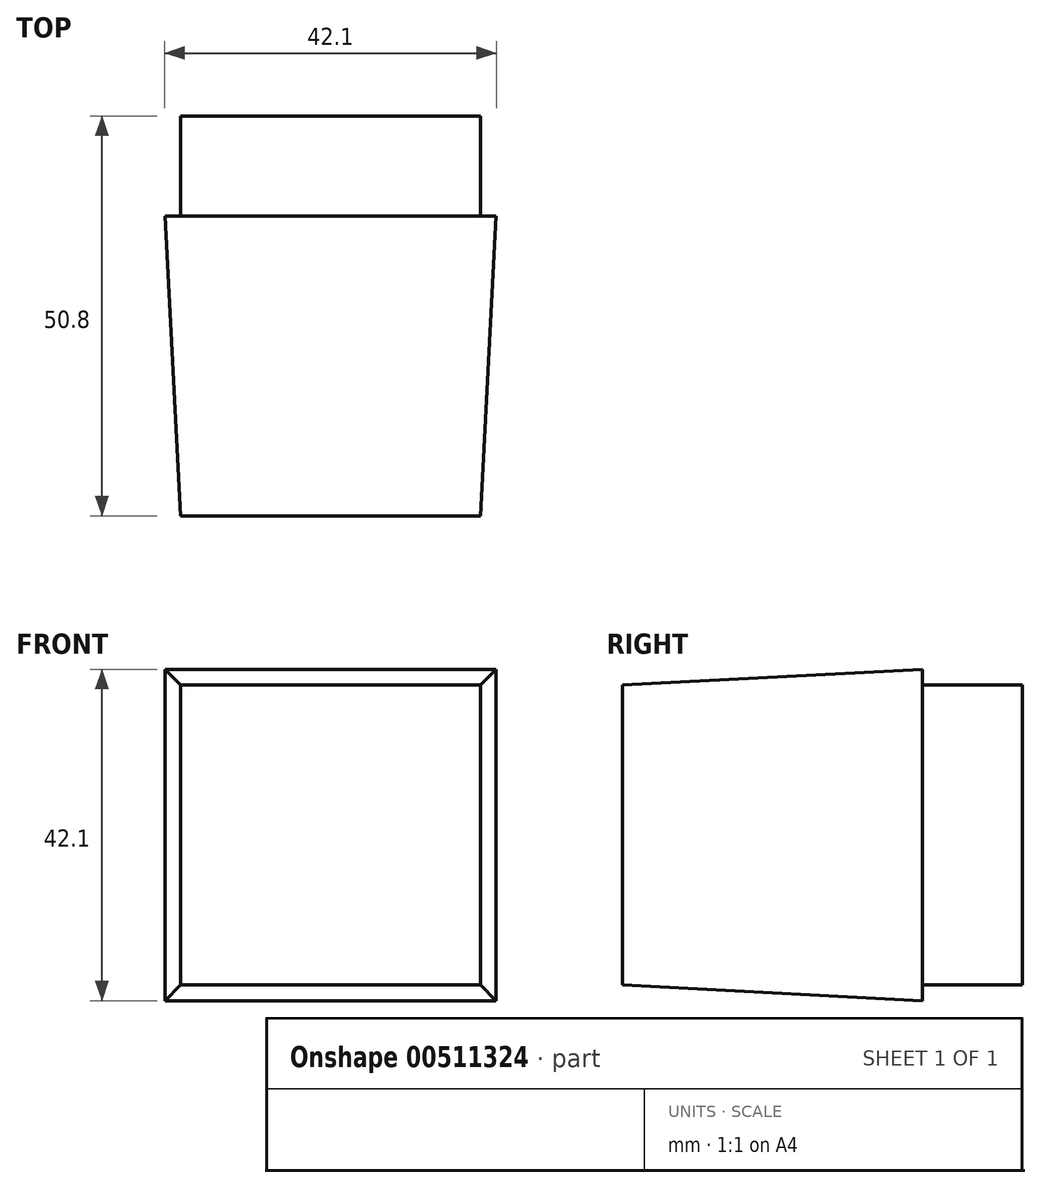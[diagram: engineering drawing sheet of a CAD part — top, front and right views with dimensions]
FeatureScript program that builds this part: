
annotation { "Feature Type Name" : "Feature", "Feature Type Description" : "" }
export const myFeature = defineFeature(function(context is Context, id is Id, definition is map)
    precondition{}
    {
        {
            var Q0;
            Q0=qCreatedBy(makeId("Front.planeOp"),FACE);
            var sketch = newSketch(context, id + "F0", { "sketchPlane" : qUnion([Q0])});
            skLineSegment(sketch, "E0", {"start": v(0, 0) * mm, "end": v(0, 38.1) * mm});
            skLineSegment(sketch, "E1", {"start": v(0, 38.1) * mm, "end": v(38.1, 38.1) * mm});
            skLineSegment(sketch, "E2", {"start": v(38.1, 38.1) * mm, "end": v(38.1, 0) * mm});
            skLineSegment(sketch, "E3", {"start": v(38.1, 0) * mm, "end": v(0, 0) * mm});
            skSolve(sketch);
        }
        {
            var Q0;
            Q0=makeQuery(id+"F0.imprint","IMPRINT",FACE,{"disambiguationData":[TD([[makeQuery(id+"F0.imprint","IMPRINT",EDGE,{"derivedFrom":sQuery(id+"F0.wireOp",EDGE,"E0")}),-1.0]])]});
            extrude(context, id + "F1", {"entities" : qUnion([Q0]), "depth" : 50.8 * mm, "offsetDistance" : 25.4 * mm});
        }
        {
            var Q0;
            Q0=makeQuery(id+"F1.opExtrude","CAP_FACE",FACE,{"disambiguationData":[OSD([sQuery(id+"F0.wireOp",EDGE,"E0"),sQuery(id+"F0.wireOp",EDGE,"E1"),sQuery(id+"F0.wireOp",EDGE,"E2"),sQuery(id+"F0.wireOp",EDGE,"E3")])],"isStart":false});
            var sketch = newSketch(context, id + "F2", { "sketchPlane" : qUnion([Q0])});
            skSolve(sketch);
        }
        {
            var Q0;
            Q0 = qSketchRegion(id + "F2", true);
            var Q1;
            Q1=makeQuery(id+"F2.imprint","IMPRINT",FACE,{"disambiguationData":[TD([[makeQuery(id+"F2.imprint","IMPRINT",EDGE,{"derivedFrom":makeQuery(id+"F1.opExtrude","CAP_EDGE",EDGE,{"disambiguationData":[OSD([sQuery(id+"F0.wireOp",EDGE,"E0")])],"isStart":false})}),-1.0]])]});
            extrude(context, id + "F3", {"entities" : qUnion([Q0, Q1]), "operationType" : NewBodyOperationType.ADD, "oppositeDirection" : true, "depth" : 38.1 * mm, "offsetDistance" : 25.4 * mm, "hasDraft" : true, "draftAngle" : 3 * degree});
        }
    });
